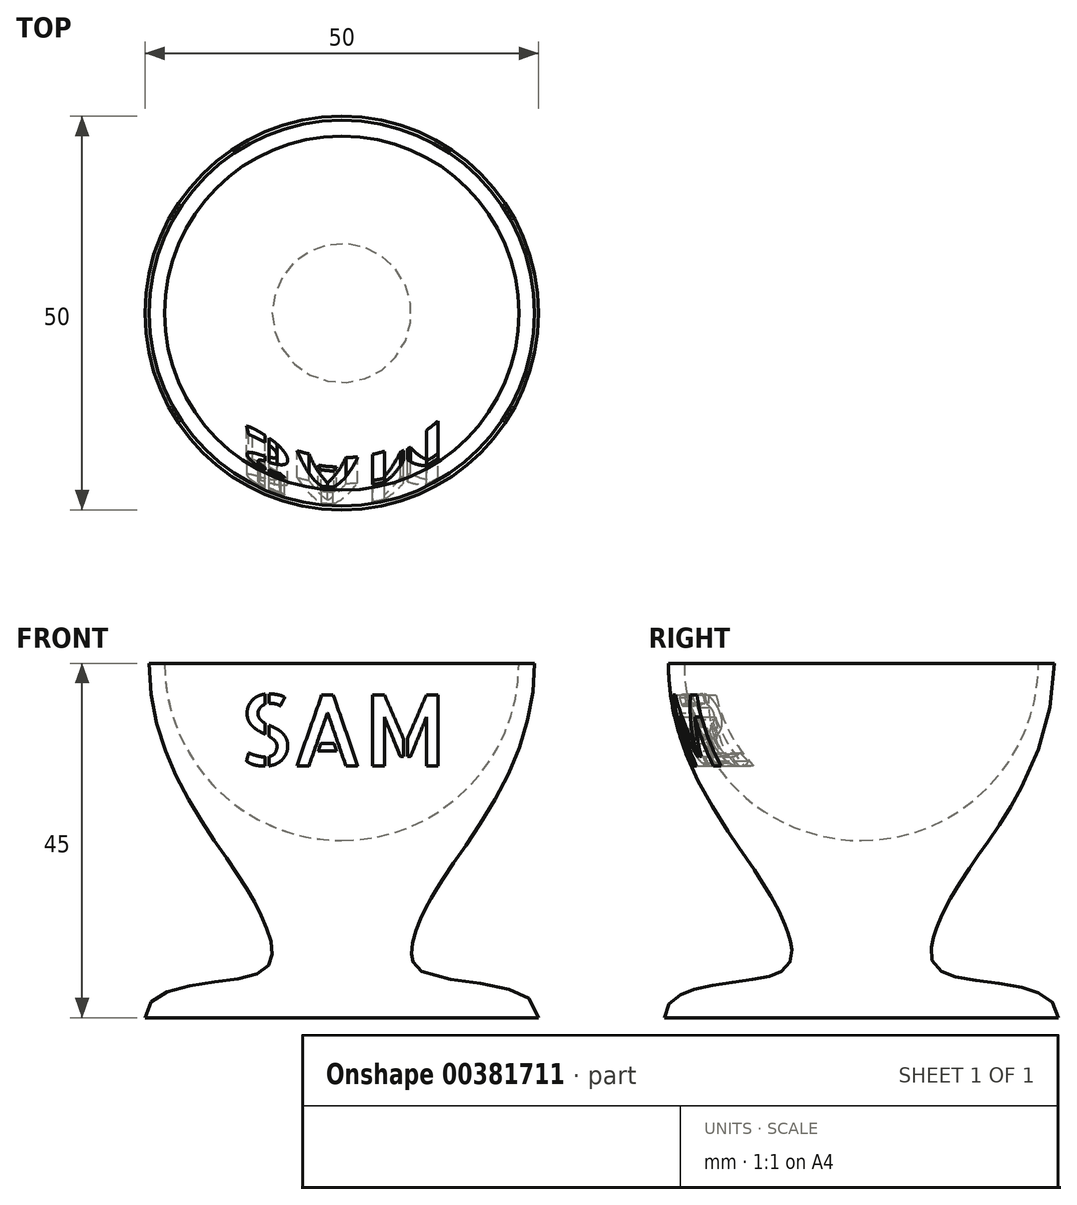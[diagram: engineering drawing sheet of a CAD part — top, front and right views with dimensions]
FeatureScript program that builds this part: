
annotation { "Feature Type Name" : "Feature", "Feature Type Description" : "" }
export const myFeature = defineFeature(function(context is Context, id is Id, definition is map)
    precondition{}
    {
        {
            var Q0;
            Q0=qCreatedBy(makeId("Front.planeOp"),FACE);
            var sketch = newSketch(context, id + "F0", { "sketchPlane" : qUnion([Q0])});
            skLineSegment(sketch, "E0", {"start": v(-25, 0) * mm, "end": v(0, 0) * mm});
            skLineSegment(sketch, "E1", {"start": v(0, 0) * mm, "end": v(0, 45) * mm});
            skCircle(sketch, "E2", {"center": v(0, 45) * mm, "radius": 22.5 * mm});
            skLineSegment(sketch, "E3", {"start": v(-22.5, 45) * mm, "end": v(-24.5, 45) * mm});
            skFitSpline(sketch, "E4", {"points": [v(-24.5, 45) * mm, v(-14.46, 20.03) * mm, v(-9.46, 11.14) * mm, v(-10.35, 5.77) * mm, v(-25, 0) * mm], "startDerivative": vector(0.05, -93.93) * mm, "endDerivative": vector(-0.5, -57.27) * mm});
            skSolve(sketch);
        }
        {
            var Q0;
            {var subQ4=sQuery(id+"F0.wireOp",EDGE,"E0");Q0=makeQuery(id+"F0.imprint","IMPRINT",FACE,{"disambiguationData":[TD([[makeQuery(id+"F0.imprint","IMPRINT",EDGE,{"derivedFrom":subQ4}),1.0]])]});}
            var Q1;
            Q1=sQuery(id+"F0.wireOp",EDGE,"E1");
            revolve(context, id + "F1", {"entities" : qUnion([Q0]), "axis" : qUnion([Q1]), "revolveType" : RevolveType.FULL});
        }
        {
            var Q0;
            Q0=qCreatedBy(makeId("Front.planeOp"),FACE);
            var sketch = newSketch(context, id + "F2", { "sketchPlane" : qUnion([Q0])});
            skText(sketch, "E5", { "text": "SAM", "fontName": "AllertaStencil-Regular.ttf"});
            skLineSegment(sketch, "E6", {"start": v(0, 32) * mm, "end": v(0, 0) * mm, "construction": true});
            const initialGuessF2  = {"E5": [-0.01308, 0.032, 1, 0, 0.009]};
            skSetInitialGuess(sketch, initialGuessF2);
            skSolve(sketch);
        }
        {
            var Q0;
            Q0=qSketchRegion(id+"F2",true);
            extrude(context, id + "F3", {"entities" : qUnion([Q0]), "operationType" : NewBodyOperationType.REMOVE, "depth" : 28.2 * mm});
        }
    });
